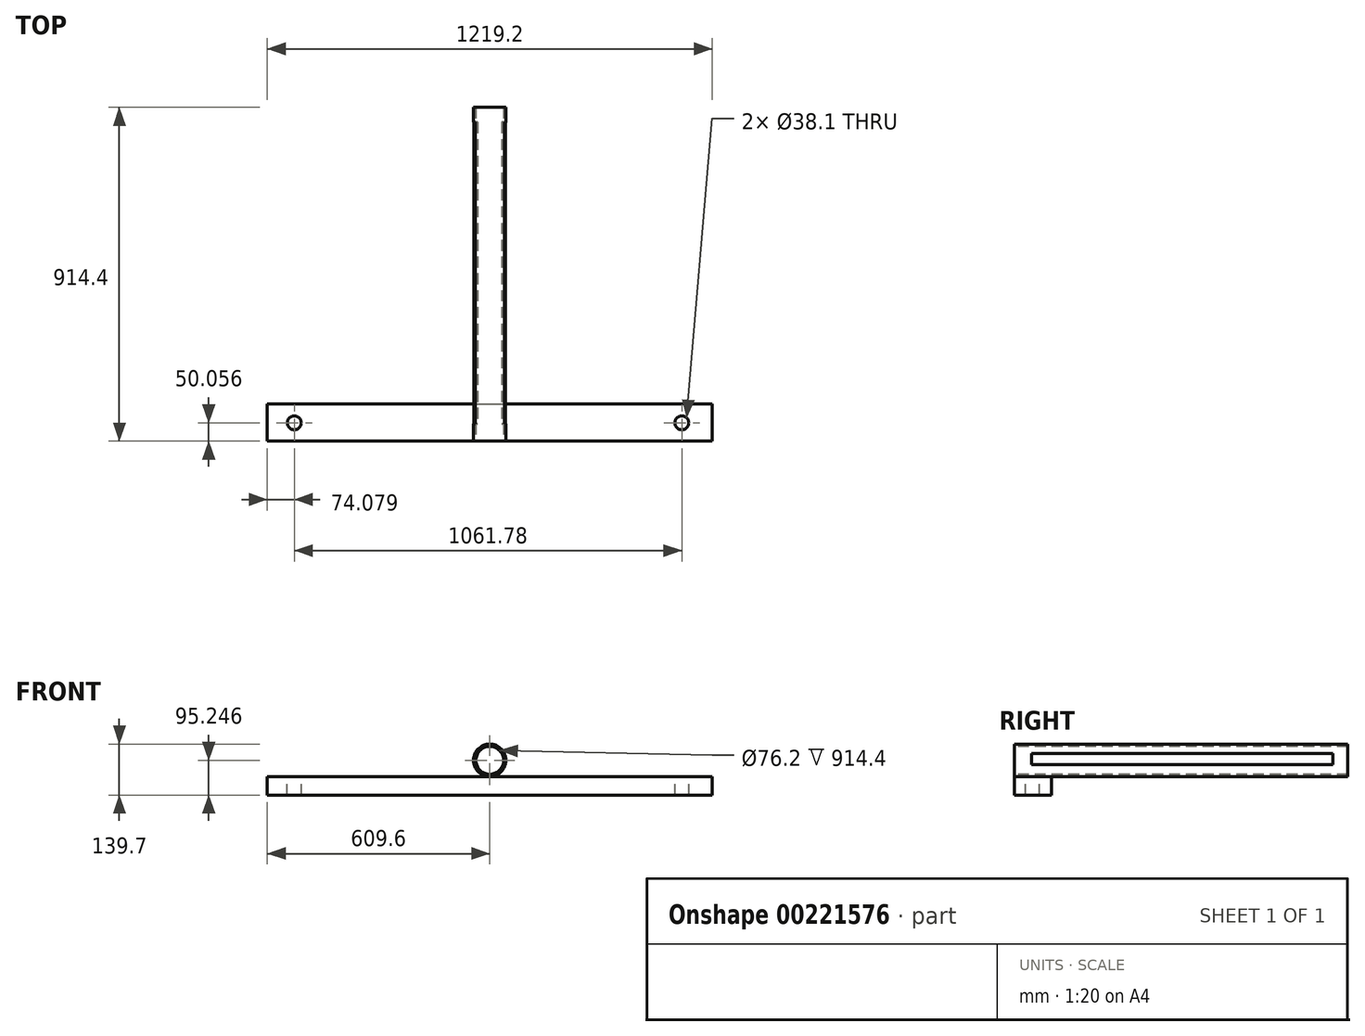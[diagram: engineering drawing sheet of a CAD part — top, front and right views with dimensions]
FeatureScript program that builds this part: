
annotation { "Feature Type Name" : "Feature", "Feature Type Description" : "" }
export const myFeature = defineFeature(function(context is Context, id is Id, definition is map)
    precondition{}
    {
        {
            var Q0;
            Q0=qCreatedBy(makeId("Front.planeOp"),FACE);
            var sketch = newSketch(context, id + "F0", { "sketchPlane" : qUnion([Q0])});
            skPoint(sketch, "E0", {"position": v(0, 37.96) * mm});
            skCircle(sketch, "E1", {"center": v(0, 82.4) * mm, "radius": 44.45 * mm});
            skPoint(sketch, "E2", {"position": v(0, 126.86) * mm});
            skSolve(sketch);
        }
        {
            var Q0;
            Q0=makeQuery(id+"F0.imprint","IMPRINT",FACE,{"disambiguationData":[TD([[makeQuery(id+"F0.imprint","IMPRINT",EDGE,{"derivedFrom":sQuery(id+"F0.wireOp",EDGE,"E1")}),1.0]])]});
            extrude(context, id + "F1", {"entities" : qUnion([Q0]), "depth" : 914.4 * mm});
        }
        {
            var Q0;
            Q0=makeQuery(id+"F1.opExtrude","CAP_FACE",FACE,{"disambiguationData":[OSD([sQuery(id+"F0.wireOp",EDGE,"E1")])],"isStart":false});
            var sketch = newSketch(context, id + "F2", { "sketchPlane" : qUnion([Q0])});
            skCircle(sketch, "E3", {"center": v(0, 82.4) * mm, "radius": 38.1 * mm});
            skSolve(sketch);
        }
        {
            var Q0;
            Q0=sQuery(id+"F2.wireOp",VERTEX,"E3.center");
            var Q1;
            Q1=makeQuery(id+"F1.opExtrude","SWEPT_BODY",BODY,{"disambiguationData":[OSD([sQuery(id+"F0.wireOp",EDGE,"E1")])]});
            hole(context, id + "F3", {"style" : HoleStyle.SIMPLE, "endStyle" : HoleEndStyle.THROUGH, "holeDiameter" : 76.2 * mm, "locations" : qUnion([Q0]), "scope" : qUnion([Q1]), "isTappedThrough" : true});
        }
        {
            var Q0;
            Q0=makeQuery(id+"F1.opExtrude","CAP_FACE",FACE,{"disambiguationData":[OSD([sQuery(id+"F0.wireOp",EDGE,"E1")])],"isStart":false});
            var sketch = newSketch(context, id + "F4", { "sketchPlane" : qUnion([Q0])});
            skLineSegment(sketch, "E4.bottom", {"start": v(-609.6, 37.96) * mm, "end": v(609.6, 37.96) * mm});
            skLineSegment(sketch, "E4.top", {"start": v(-609.6, -12.84) * mm, "end": v(609.6, -12.84) * mm});
            skLineSegment(sketch, "E4.left", {"start": v(-609.6, 37.96) * mm, "end": v(-609.6, -12.84) * mm});
            skLineSegment(sketch, "E4.right", {"start": v(609.6, 37.96) * mm, "end": v(609.6, -12.84) * mm});
            skPoint(sketch, "E4.middle", {"position": v(0, 12.56) * mm});
            skPoint(sketch, "E5", {"position": v(0, 37.96) * mm});
            skSolve(sketch);
        }
        {
            var Q0;
            Q0=makeQuery(id+"F4.imprint","IMPRINT",FACE,{"disambiguationData":[TD([[makeQuery(id+"F4.imprint","IMPRINT",EDGE,{"derivedFrom":sQuery(id+"F4.wireOp",EDGE,"E4.top")}),1.0]])]});
            extrude(context, id + "F5", {"entities" : qUnion([Q0]), "operationType" : NewBodyOperationType.ADD, "oppositeDirection" : true, "depth" : 101.6 * mm});
        }
        {
            var Q0;
            Q0=makeQuery(id+"F5.opExtrude","SWEPT_FACE",FACE,{"disambiguationData":[OSD([sQuery(id+"F4.wireOp",EDGE,"E4.bottom")])]});
            var sketch = newSketch(context, id + "F6", { "sketchPlane" : qUnion([Q0])});
            skPoint(sketch, "E6", {"position": v(-535.52, -864.34) * mm});
            skPoint(sketch, "E7", {"position": v(-609.6, -864.34) * mm});
            skPoint(sketch, "E8", {"position": v(526.26, -864.34) * mm});
            skPoint(sketch, "E9", {"position": v(609.6, -864.34) * mm});
            skSolve(sketch);
        }
        {
            var Q0;
            Q0=sQuery(id+"F6.wireOp",VERTEX,"E6");
            var Q1;
            Q1=makeQuery(id+"F5.opExtrude","SWEPT_BODY",BODY,{"disambiguationData":[OSD([sQuery(id+"F4.wireOp",EDGE,"E4.bottom"),sQuery(id+"F4.wireOp",EDGE,"E4.top"),sQuery(id+"F4.wireOp",EDGE,"E4.left"),sQuery(id+"F4.wireOp",EDGE,"E4.right")])]});
            hole(context, id + "F7", {"style" : HoleStyle.SIMPLE, "endStyle" : HoleEndStyle.THROUGH, "holeDiameter" : 38.1 * mm, "locations" : qUnion([Q0]), "scope" : qUnion([Q1]), "isTappedThrough" : true});
        }
        {
            var Q0;
            Q0=sQuery(id+"F6.wireOp",VERTEX,"E8");
            var Q1;
            Q1=makeQuery(id+"F5.opExtrude","SWEPT_BODY",BODY,{"disambiguationData":[OSD([sQuery(id+"F4.wireOp",EDGE,"E4.bottom"),sQuery(id+"F4.wireOp",EDGE,"E4.top"),sQuery(id+"F4.wireOp",EDGE,"E4.left"),sQuery(id+"F4.wireOp",EDGE,"E4.right")])]});
            hole(context, id + "F8", {"style" : HoleStyle.SIMPLE, "endStyle" : HoleEndStyle.THROUGH, "holeDiameter" : 38.1 * mm, "locations" : qUnion([Q0]), "scope" : qUnion([Q1]), "isTappedThrough" : true});
        }
        {
            var Q0;
            Q0=qCreatedBy(makeId("Right.planeOp"),FACE);
            var sketch = newSketch(context, id + "F9", { "sketchPlane" : qUnion([Q0])});
            skLineSegment(sketch, "E10.bottom", {"start": v(-866.86, 101.45) * mm, "end": v(-40.97, 101.45) * mm});
            skLineSegment(sketch, "E10.top", {"start": v(-866.86, 71.2) * mm, "end": v(-40.97, 71.2) * mm});
            skLineSegment(sketch, "E10.left", {"start": v(-866.86, 101.45) * mm, "end": v(-866.86, 71.2) * mm});
            skLineSegment(sketch, "E10.right", {"start": v(-40.97, 101.45) * mm, "end": v(-40.97, 71.2) * mm});
            skSolve(sketch);
        }
        {
            var Q0;
            Q0=makeQuery(id+"F9.imprint","IMPRINT",FACE,{"disambiguationData":[TD([[makeQuery(id+"F9.imprint","IMPRINT",EDGE,{"derivedFrom":sQuery(id+"F9.wireOp",EDGE,"E10.bottom")}),-1.0]])]});
            extrude(context, id + "F10", {"entities" : qUnion([Q0]), "operationType" : NewBodyOperationType.REMOVE, "oppositeDirection" : true, "depth" : 114.3 * mm});
        }
        {
            var Q0;
            Q0 = qSketchRegion(id + "F9", true);
            extrude(context, id + "F11", {"entities" : qUnion([Q0]), "operationType" : NewBodyOperationType.REMOVE, "depth" : 109.22 * mm});
        }
    });
